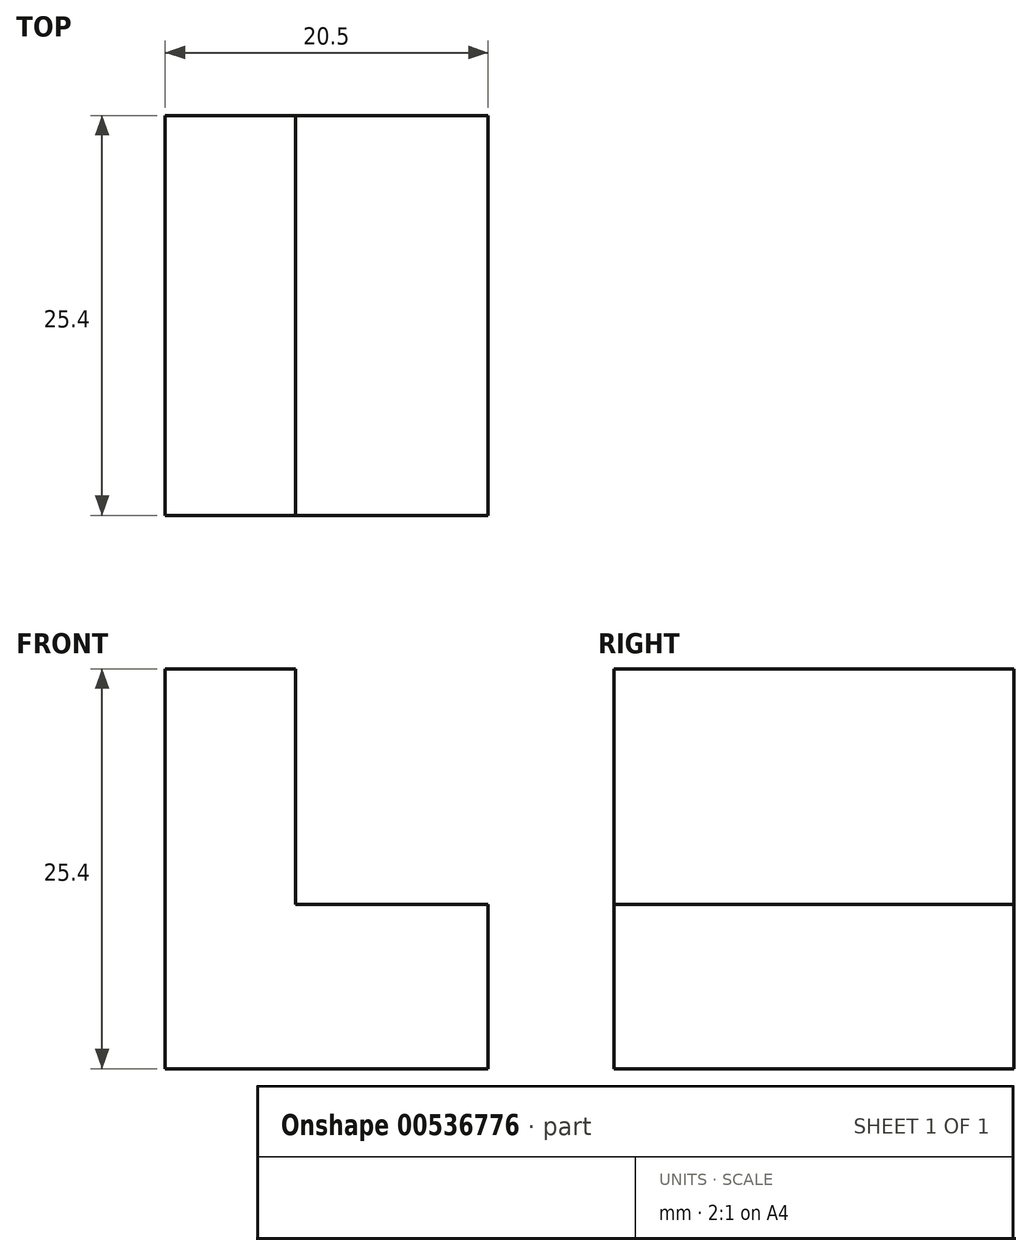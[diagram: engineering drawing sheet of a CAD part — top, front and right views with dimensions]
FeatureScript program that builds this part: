
annotation { "Feature Type Name" : "Feature", "Feature Type Description" : "" }
export const myFeature = defineFeature(function(context is Context, id is Id, definition is map)
    precondition{}
    {
        {
            var Q0;
            Q0=qCreatedBy(makeId("Front.planeOp"),FACE);
            var sketch = newSketch(context, id + "F0", { "sketchPlane" : qUnion([Q0])});
            skLineSegment(sketch, "E0", {"start": v(0, 0) * mm, "end": v(0, 25.4) * mm});
            skLineSegment(sketch, "E1", {"start": v(0, 25.4) * mm, "end": v(8.28, 25.4) * mm});
            skLineSegment(sketch, "E2", {"start": v(8.28, 25.4) * mm, "end": v(8.28, 10.44) * mm});
            skLineSegment(sketch, "E3", {"start": v(8.28, 10.44) * mm, "end": v(20.5, 10.44) * mm});
            skLineSegment(sketch, "E4", {"start": v(20.5, 10.44) * mm, "end": v(20.5, 0) * mm});
            skLineSegment(sketch, "E5", {"start": v(20.5, 0) * mm, "end": v(0, 0) * mm});
            skSolve(sketch);
        }
        {
            var Q0;
            Q0 = qSketchRegion(id + "F0", true);
            extrude(context, id + "F1", {"entities" : qUnion([Q0]), "depth" : 25.4 * mm, "offsetDistance" : 25.4 * mm});
        }
    });
